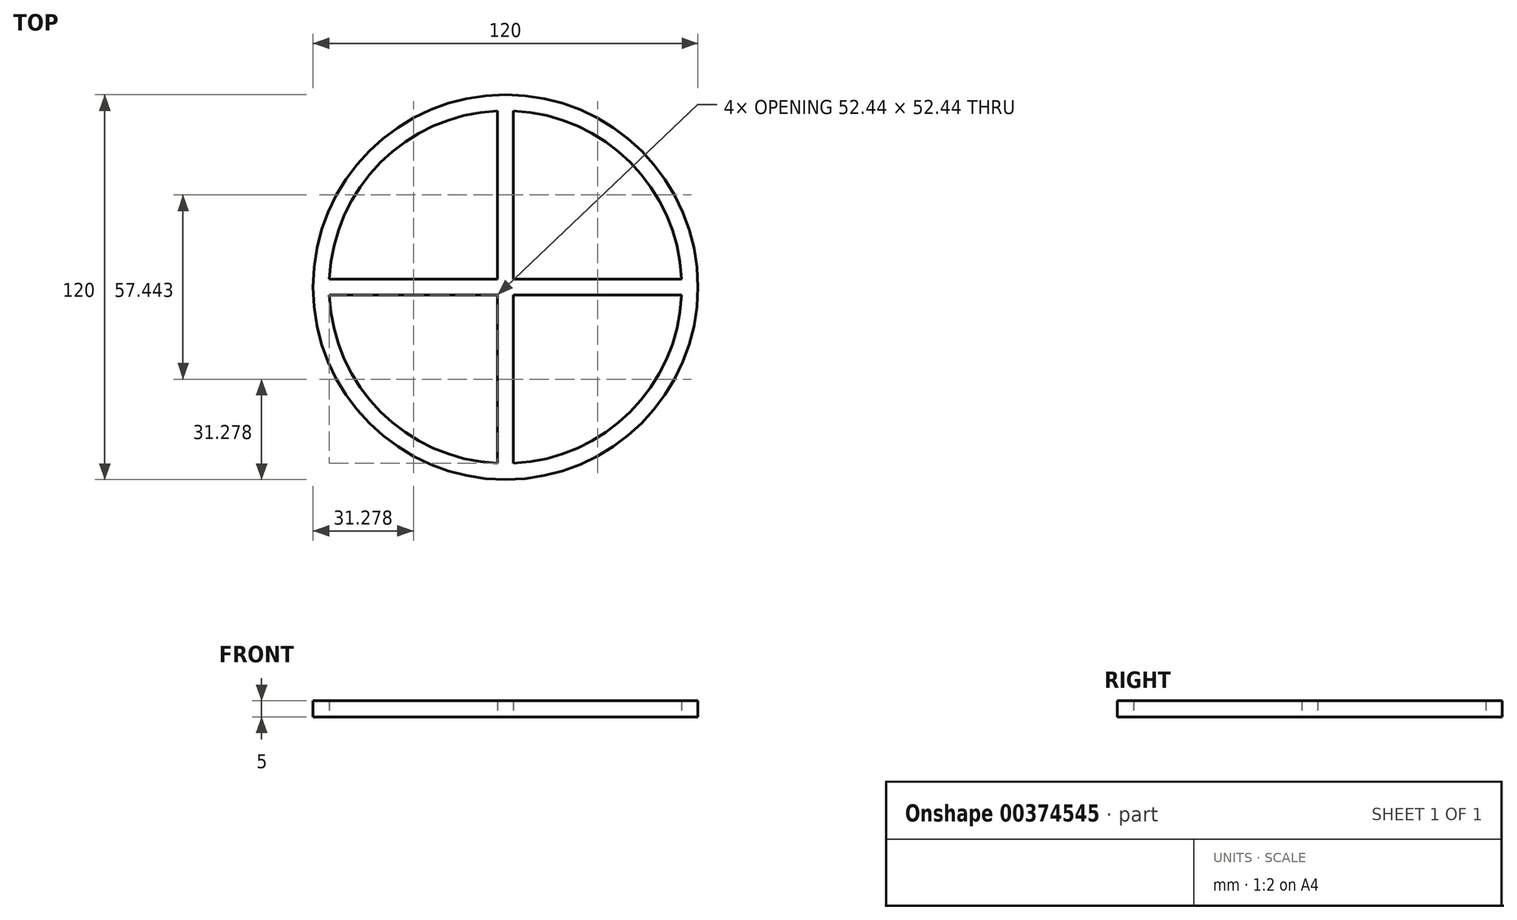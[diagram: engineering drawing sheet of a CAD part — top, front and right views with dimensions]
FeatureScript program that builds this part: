
annotation { "Feature Type Name" : "Feature", "Feature Type Description" : "" }
export const myFeature = defineFeature(function(context is Context, id is Id, definition is map)
    precondition{}
    {
        {
            var Q0;
            Q0=qCreatedBy(makeId("Top.planeOp"),FACE);
            var sketch = newSketch(context, id + "F0", { "sketchPlane" : qUnion([Q0])});
            skCircle(sketch, "E0", {"center": v(0, 0) * mm, "radius": 60 * mm});
            skArc(sketch, "E1", {"start": v(54.94, 2.5) * mm, "mid": v(38.9, 38.9) * mm, "end": v(2.5, 54.94) * mm});
            skArc(sketch, "E2.trimOffspring", {"start": v(-54.94, -2.5) * mm, "mid": v(-38.9, -38.9) * mm, "end": v(-2.5, -54.94) * mm});
            skArc(sketch, "E3.trimOffspring", {"start": v(-2.5, 54.94) * mm, "mid": v(-38.9, 38.9) * mm, "end": v(-54.94, 2.5) * mm});
            skArc(sketch, "E4.trimOffspring", {"start": v(2.5, -54.94) * mm, "mid": v(38.9, -38.9) * mm, "end": v(54.94, -2.5) * mm});
            skLineSegment(sketch, "E5", {"start": v(2.5, 54.94) * mm, "end": v(2.5, 2.5) * mm});
            skLineSegment(sketch, "E6", {"start": v(-2.5, 54.94) * mm, "end": v(-2.5, 2.5) * mm});
            skLineSegment(sketch, "E7.trimOffspring", {"start": v(2.5, -2.5) * mm, "end": v(2.5, -54.94) * mm});
            skLineSegment(sketch, "E8.trimOffspring", {"start": v(-2.5, -2.5) * mm, "end": v(-2.5, -54.94) * mm});
            skLineSegment(sketch, "E9", {"start": v(-54.94, -2.5) * mm, "end": v(-2.5, -2.5) * mm});
            skLineSegment(sketch, "E10", {"start": v(-54.94, 2.5) * mm, "end": v(-2.5, 2.5) * mm});
            skLineSegment(sketch, "E11.trimOffspring", {"start": v(2.5, 2.5) * mm, "end": v(54.96, 2.5) * mm});
            skLineSegment(sketch, "E12.trimOffspring", {"start": v(2.5, -2.5) * mm, "end": v(54.94, -2.5) * mm});
            skSolve(sketch);
        }
        {
            var Q0;
            Q0=makeQuery(id+"F0.imprint","IMPRINT",FACE,{"disambiguationData":[TD([[makeQuery(id+"F0.imprint","IMPRINT",EDGE,{"derivedFrom":sQuery(id+"F0.wireOp",EDGE,"E0")}),1.0]])]});
            extrude(context, id + "F1", {"entities" : qUnion([Q0]), "depth" : 5 * mm});
        }
    });
